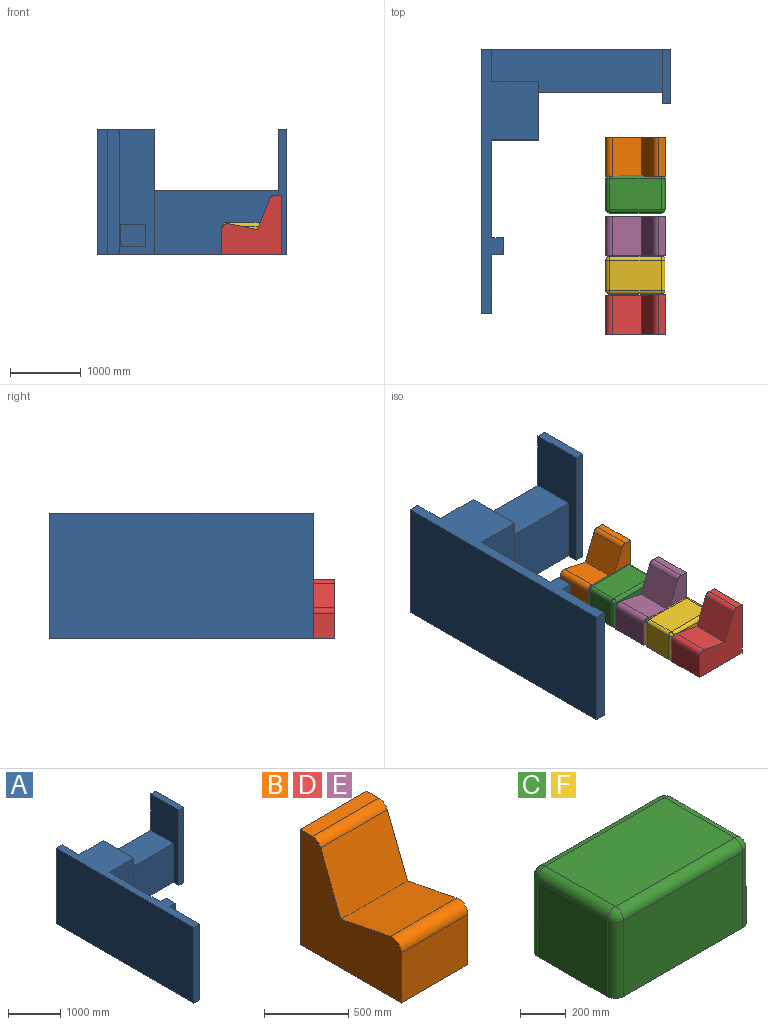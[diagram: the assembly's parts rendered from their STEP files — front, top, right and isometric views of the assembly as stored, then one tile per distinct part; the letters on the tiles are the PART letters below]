
ASSEMBLY  parts=6 mates=3
PART A: 26 faces, bbox 2692.4x3737.5x1778 mm
  f0: plane 346.64x76.2mm, normal (0,0,1), area 26414mm2, adj f1,f22,f23,f25
  f1: plane 1778x660.4mm, normal (0,-1,0), area 1066016.5mm2, adj f0,f3,f4,f5,f13,f21,f22,f23
  f2: plane 863.6x660.4mm, normal (0,1,0), area 570321.4mm2, adj f3,f4,f12,f19
  f3: plane 1778x825.5mm, normal (1,0,0), area 1328384.4mm2, adj f1,f2,f4,f5,f11,f12
  f4: plane 3737.55x812.8mm, normal (0,0,1), area 1154600.9mm2, adj f1,f2,f3,f7,f13,f14,f15,f16
  f5: plane 3737.55x2692.4mm, normal (0,0,-1), area 2542452.8mm2, adj f1,f3,f6,f7,f8,f9,f11,f13
  f6: plane 1778x762mm, normal (1,0,0), area 1354836mm2, adj f5,f7,f9,f10
  f7: plane 2692.4x1778mm, normal (0,1,0), area 2703220.4mm2, adj f4,f5,f6,f8,f10,f12,f14,f19
  f8: plane 1778x762mm, normal (-1,0,0), area 797417.8mm2, adj f5,f7,f9,f10,f11,f12
  f9: plane 1778x127mm, normal (0,-1,0), area 225806mm2, adj f5,f6,f8,f10
  f10: plane 762x127mm, normal (0,0,1), area 96774mm2, adj f6,f7,f8,f9
  f11: plane 1752.6x914.4mm, normal (0,-1,0), area 1602577.4mm2, adj f3,f5,f8,f12
  f12: plane 2413x609.6mm, normal (0,0,1), area 1370319.8mm2, adj f2,f3,f7,f8,f11,f19
  f13: plane 1778x1384.3mm, normal (1,0,0), area 2461285.4mm2, adj f1,f4,f5,f20
  f14: plane 3737.55x1778mm, normal (-1,0,0), area 6645357mm2, adj f4,f5,f7,f15
  f15: plane 1778x152.4mm, normal (0,-1,0), area 270967.2mm2, adj f4,f5,f14,f16
  f16: plane 1778x829.25mm, normal (1,0,0), area 1474399.6mm2, adj f4,f5,f15,f17
  f17: plane 1778x165.1mm, normal (0,-1,0), area 293547.8mm2, adj f4,f5,f16,f18
  f18: plane 1778x241.3mm, normal (1,0,0), area 429031.4mm2, adj f4,f5,f17,f20
  f19: plane 863.6x457.2mm, normal (1,0,0), area 394837.9mm2, adj f2,f4,f7,f12
  f20: plane 1778x165.1mm, normal (0,1,0), area 293547.8mm2, adj f4,f5,f13,f18
  f21: plane 346.64x304.8mm, normal (0,0,-1), area 105655.9mm2, adj f1,f22,f23,f24
  f22: plane 435.4x304.8mm, normal (1,0,0), area 123312.9mm2, adj f0,f1,f5,f21,f24,f25
  f23: plane 435.4x304.8mm, normal (-1,0,0), area 123312.9mm2, adj f0,f1,f5,f21,f24,f25
  f24: plane 435.4x346.64mm, normal (0,-1,0), area 150928.6mm2, adj f5,f21,f22,f23
  f25: plane 346.64x123.34mm, normal (0,1,0), area 42753.9mm2, adj f0,f5,f22,f23
PART B: 10 faces, bbox 558.8x850.9x838.2 mm
  f0: plane 558.8x416.86mm, normal (0,0.2,0.98), area 237552.2mm2, adj f1,f7,f8,f9
  f1: cylinder r=76.2mm len=558.8mm, axis (-1,0,0), area 75290.6mm2, adj f0,f2,f8,f9
  f2: plane 558.8x364.25mm, normal (0,-1,0), area 203543.4mm2, adj f1,f3,f8,f9
  f3: plane 850.9x558.8mm, normal (0,0,-1), area 475482.9mm2, adj f2,f4,f8,f9
  f4: plane 838.2x558.8mm, normal (0,1,0), area 468386.2mm2, adj f3,f5,f8,f9
  f5: plane 558.8x102.58mm, normal (0,0,1), area 57320.5mm2, adj f4,f6,f8,f9
  f6: cylinder r=76.2mm len=558.8mm, axis (-1,0,0), area 51048.5mm2, adj f5,f7,f8,f9
  f7: plane 558.8x434.09mm, normal (0,-0.93,0.36), area 260372.8mm2, adj f0,f6,f8,f9
  f8: plane 850.9x838.2mm, normal (1,0,0), area 446008mm2, adj f0,f1,f2,f3,f4,f5,f6,f7
  f9: plane 850.9x838.2mm, normal (-1,0,0), area 446008mm2, adj f0,f1,f2,f3,f4,f5,f6,f7
PART C: 18 faces, bbox 838.2x533.4x457.2 mm
  f0: plane 431.8x406.4mm, normal (1,0,0), area 175483.5mm2, adj f5,f8,f14,f17
  f1: plane 736.6x406.4mm, normal (0,1,0), area 299354.2mm2, adj f5,f11,f15,f17
  f2: plane 431.8x406.4mm, normal (-1,0,0), area 175483.5mm2, adj f5,f6,f10,f11
  f3: plane 736.6x406.4mm, normal (0,-1,0), area 299354.2mm2, adj f5,f6,f8,f9
  f4: plane 736.6x431.8mm, normal (0,0,1), area 318063.9mm2, adj f9,f10,f14,f15
  f5: plane 838.2x533.4mm, normal (0,0,-1), area 444880.6mm2, adj f0,f1,f2,f3,f6,f8,f11,f17
  f6: cylinder r=50.8mm len=406.4mm, axis (0,0,1), area 32429.3mm2, adj f2,f3,f5,f7
  f7: sphere r=50.8mm, area 4053.7mm2, adj f6,f9,f10
  f8: cylinder r=50.8mm len=406.4mm, axis (0,0,-1), area 32429.3mm2, adj f0,f3,f5,f12
  f9: cylinder r=50.8mm len=736.6mm, axis (-1,0,0), area 58778.1mm2, adj f3,f4,f7,f12
  f10: cylinder r=50.8mm len=431.8mm, axis (0,1,0), area 34456.1mm2, adj f2,f4,f7,f13
  f11: cylinder r=50.8mm len=406.4mm, axis (0,0,-1), area 32429.3mm2, adj f1,f2,f5,f13
  f12: sphere r=50.8mm, area 4053.7mm2, adj f8,f9,f14
  f13: sphere r=50.8mm, area 4053.7mm2, adj f10,f11,f15
  f14: cylinder r=50.8mm len=431.8mm, axis (0,-1,0), area 34456.1mm2, adj f0,f4,f12,f16
  f15: cylinder r=50.8mm len=736.6mm, axis (1,0,0), area 58778.1mm2, adj f1,f4,f13,f16
  f16: sphere r=50.8mm, area 4053.7mm2, adj f14,f15,f17
  f17: cylinder r=50.8mm len=406.4mm, axis (0,0,1), area 32429.3mm2, adj f0,f1,f5,f16
PART D: same geometry as B
PART E: same geometry as B
PART F: same geometry as C
PLACE A t=(-1752.6,0,0)mm
PLACE B rot(axis=(0,0,-1),90deg) t=(52.44,-912.27,0)mm
PLACE C t=(-376.63,-1438.79,0)mm
PLACE D rot(axis=(0,0,-1),90deg) t=(52.44,-3147.47,0)mm
PLACE E rot(axis=(0,0,-1),90deg) t=(52.44,-2029.87,0)mm
PLACE F t=(-377.07,-2588.32,0)mm
MATE planar F.f5 <-> A.f5  axis (0,0,-1) through (-377.07,-2588.32,0)mm
MATE planar C.f5 <-> A.f5  axis (0,0,-1) through (-376.63,-1438.79,0)mm
MATE planar A.f5 <-> B.f3  axis (0,0,-1) through (-1589.85,-174.98,0)mm
